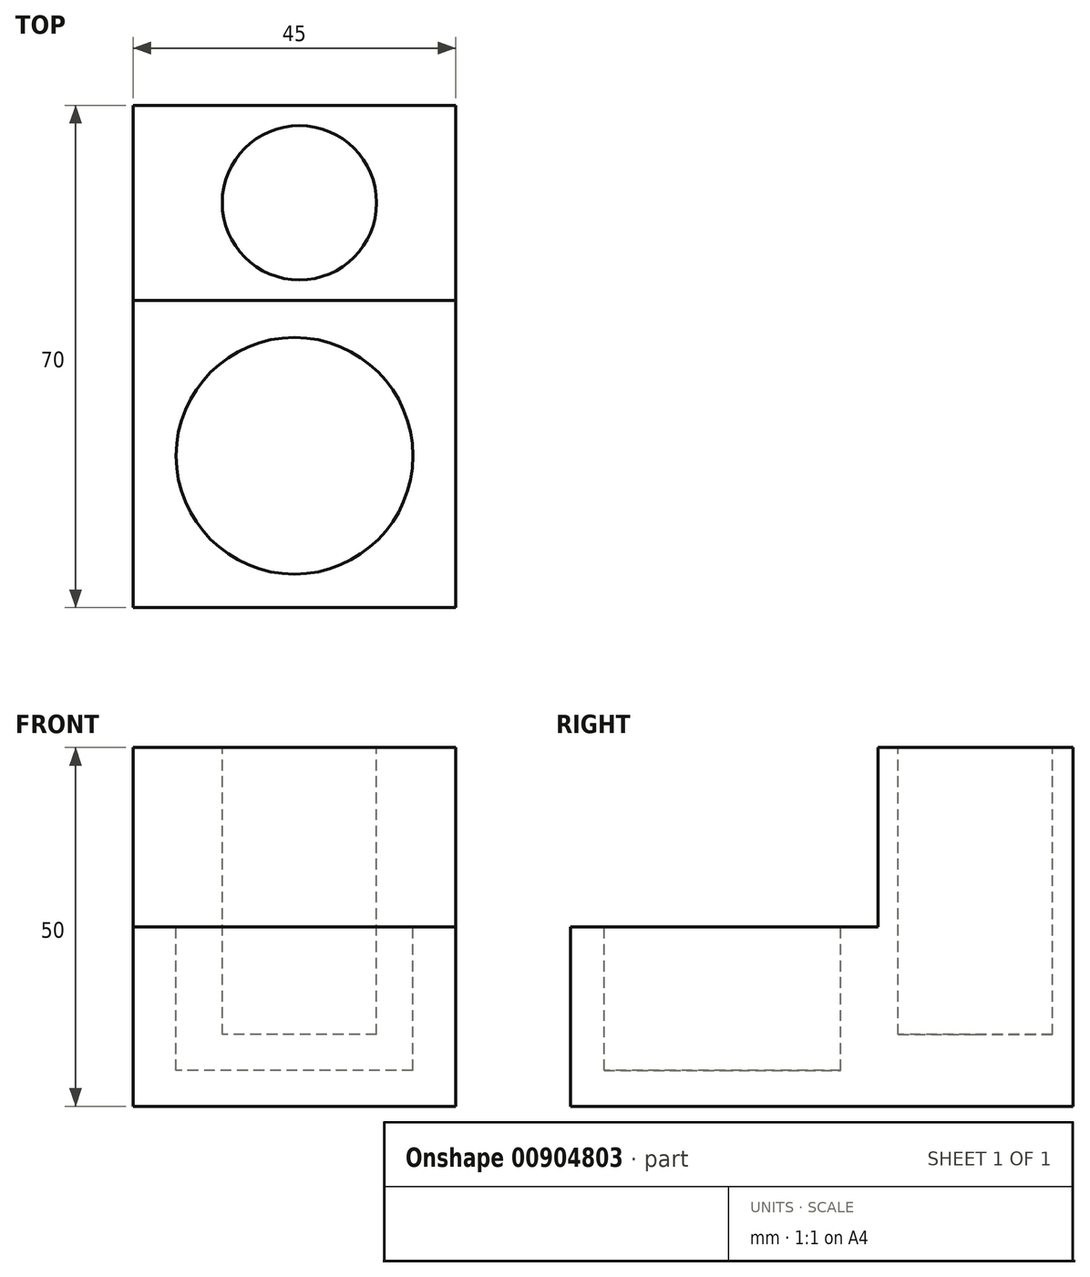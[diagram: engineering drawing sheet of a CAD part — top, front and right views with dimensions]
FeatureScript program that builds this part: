
annotation { "Feature Type Name" : "Feature", "Feature Type Description" : "" }
export const myFeature = defineFeature(function(context is Context, id is Id, definition is map)
    precondition{}
    {
        {
            var Q0;
            Q0=qCreatedBy(makeId("Top.planeOp"),FACE);
            var sketch = newSketch(context, id + "F0", { "sketchPlane" : qUnion([Q0])});
            skLineSegment(sketch, "E0", {"start": v(-23.88, -70) * mm, "end": v(21.12, -70) * mm});
            skLineSegment(sketch, "E1", {"start": v(21.12, -70) * mm, "end": v(21.12, 0) * mm});
            skLineSegment(sketch, "E2", {"start": v(-23.88, -70) * mm, "end": v(-23.88, 0) * mm});
            skLineSegment(sketch, "E3", {"start": v(-23.88, 0) * mm, "end": v(21.12, 0) * mm});
            skSolve(sketch);
        }
        {
            var Q0;
            Q0 = qSketchRegion(id + "F0", true);
            extrude(context, id + "F1", {"entities" : qUnion([Q0]), "depth" : 25 * mm, "offsetDistance" : 25 * mm});
        }
        {
            var Q0;
            Q0=makeQuery(id+"F1.opExtrude","CAP_FACE",FACE,{"disambiguationData":[OSD([sQuery(id+"F0.wireOp",EDGE,"E0"),sQuery(id+"F0.wireOp",EDGE,"E1"),sQuery(id+"F0.wireOp",EDGE,"E2"),sQuery(id+"F0.wireOp",EDGE,"E3")])],"isStart":false});
            var sketch = newSketch(context, id + "F2", { "sketchPlane" : qUnion([Q0])});
            skLineSegment(sketch, "E4", {"start": v(-1.38, -70) * mm, "end": v(-1.38, 0) * mm});
            skCircle(sketch, "E5", {"center": v(-1.38, -14.34) * mm, "radius": 10.75 * mm});
            skCircle(sketch, "E6", {"center": v(-1.38, -48.85) * mm, "radius": 16.5 * mm});
            skLineSegment(sketch, "E7", {"start": v(-1.38, -28.3) * mm, "end": v(21.12, -28.3) * mm});
            skLineSegment(sketch, "E8", {"start": v(-1.38, -28.3) * mm, "end": v(-23.88, -28.3) * mm});
            skSolve(sketch);
        }
        {
            var Q0;
            {var subQ0=sQuery(id+"F2.wireOp",EDGE,"E6");var subQ1=sQuery(id+"F2.wireOp",EDGE,"E4");var subQ2=makeQuery(id+"F2.imprint","INTERSECT",VERTEX,{"disambiguationData":[OD(0.0)],"derivedFrom":[subQ1,subQ0]});Q0=makeQuery(id+"F2.imprint","IMPRINT",FACE,{"disambiguationData":[TD([[makeQuery(id+"F2.imprint","IMPRINT",EDGE,{"disambiguationData":[TD([[subQ2,-1.0]])],"derivedFrom":subQ1}),-1.0]])]});}
            var Q1;
            {var subQ0=sQuery(id+"F2.wireOp",EDGE,"E6");var subQ1=sQuery(id+"F2.wireOp",EDGE,"E4");var subQ2=makeQuery(id+"F2.imprint","INTERSECT",VERTEX,{"disambiguationData":[OD(0.0)],"derivedFrom":[subQ1,subQ0]});Q1=makeQuery(id+"F2.imprint","IMPRINT",FACE,{"disambiguationData":[TD([[makeQuery(id+"F2.imprint","IMPRINT",EDGE,{"disambiguationData":[TD([[subQ2,-1.0]])],"derivedFrom":subQ1}),1.0]])]});}
            extrude(context, id + "F3", {"entities" : qUnion([Q0, Q1]), "operationType" : NewBodyOperationType.REMOVE, "oppositeDirection" : true, "depth" : 20 * mm, "offsetDistance" : 25 * mm});
        }
        {
            var Q0;
            Q0=makeQuery(id+"F1.opExtrude","CAP_FACE",FACE,{"disambiguationData":[OSD([sQuery(id+"F0.wireOp",EDGE,"E0"),sQuery(id+"F0.wireOp",EDGE,"E1"),sQuery(id+"F0.wireOp",EDGE,"E2"),sQuery(id+"F0.wireOp",EDGE,"E3")])],"isStart":false});
            var sketch = newSketch(context, id + "F4", { "sketchPlane" : qUnion([Q0])});
            skLineSegment(sketch, "E9", {"start": v(-23.88, -27.18) * mm, "end": v(21.12, -27.18) * mm});
            skLineSegment(sketch, "E10", {"start": v(21.12, -27.18) * mm, "end": v(0, -27.18) * mm});
            skSolve(sketch);
        }
        {
            var Q0;
            Q0 = qSketchRegion(id + "F4", true);
            var Q1;
            {var subQ3=sQuery(id+"F4.wireOp",EDGE,"E9");Q1=makeQuery(id+"F4.imprint","IMPRINT",FACE,{"disambiguationData":[TD([[makeQuery(id+"F4.imprint","IMPRINT",EDGE,{"derivedFrom":subQ3}),1.0]])]});}
            extrude(context, id + "F5", {"entities" : qUnion([Q0, Q1]), "operationType" : NewBodyOperationType.ADD, "depth" : 25 * mm, "offsetDistance" : 25 * mm});
        }
        {
            var Q0;
            Q0=makeQuery(id+"F5.opExtrude","CAP_FACE",FACE,{"disambiguationData":[OSD([sQuery(id+"F0.wireOp",EDGE,"E1"),sQuery(id+"F0.wireOp",EDGE,"E2"),sQuery(id+"F0.wireOp",EDGE,"E3"),sQuery(id+"F4.wireOp",EDGE,"E9"),sQuery(id+"F4.wireOp",EDGE,"E10")])],"isStart":false});
            var sketch = newSketch(context, id + "F6", { "sketchPlane" : qUnion([Q0])});
            skLineSegment(sketch, "E11", {"start": v(-23.88, -13.59) * mm, "end": v(21.12, -13.59) * mm});
            skLineSegment(sketch, "E12", {"start": v(-1.38, -27.18) * mm, "end": v(0, 0) * mm});
            skCircle(sketch, "E13", {"center": v(-0.69, -13.59) * mm, "radius": 10.75 * mm});
            skSolve(sketch);
        }
        {
            var Q0;
            Q0 = qSketchRegion(id + "F6", true);
            extrude(context, id + "F7", {"entities" : qUnion([Q0]), "operationType" : NewBodyOperationType.REMOVE, "oppositeDirection" : true, "depth" : 40 * mm, "offsetDistance" : 25 * mm});
        }
    });
